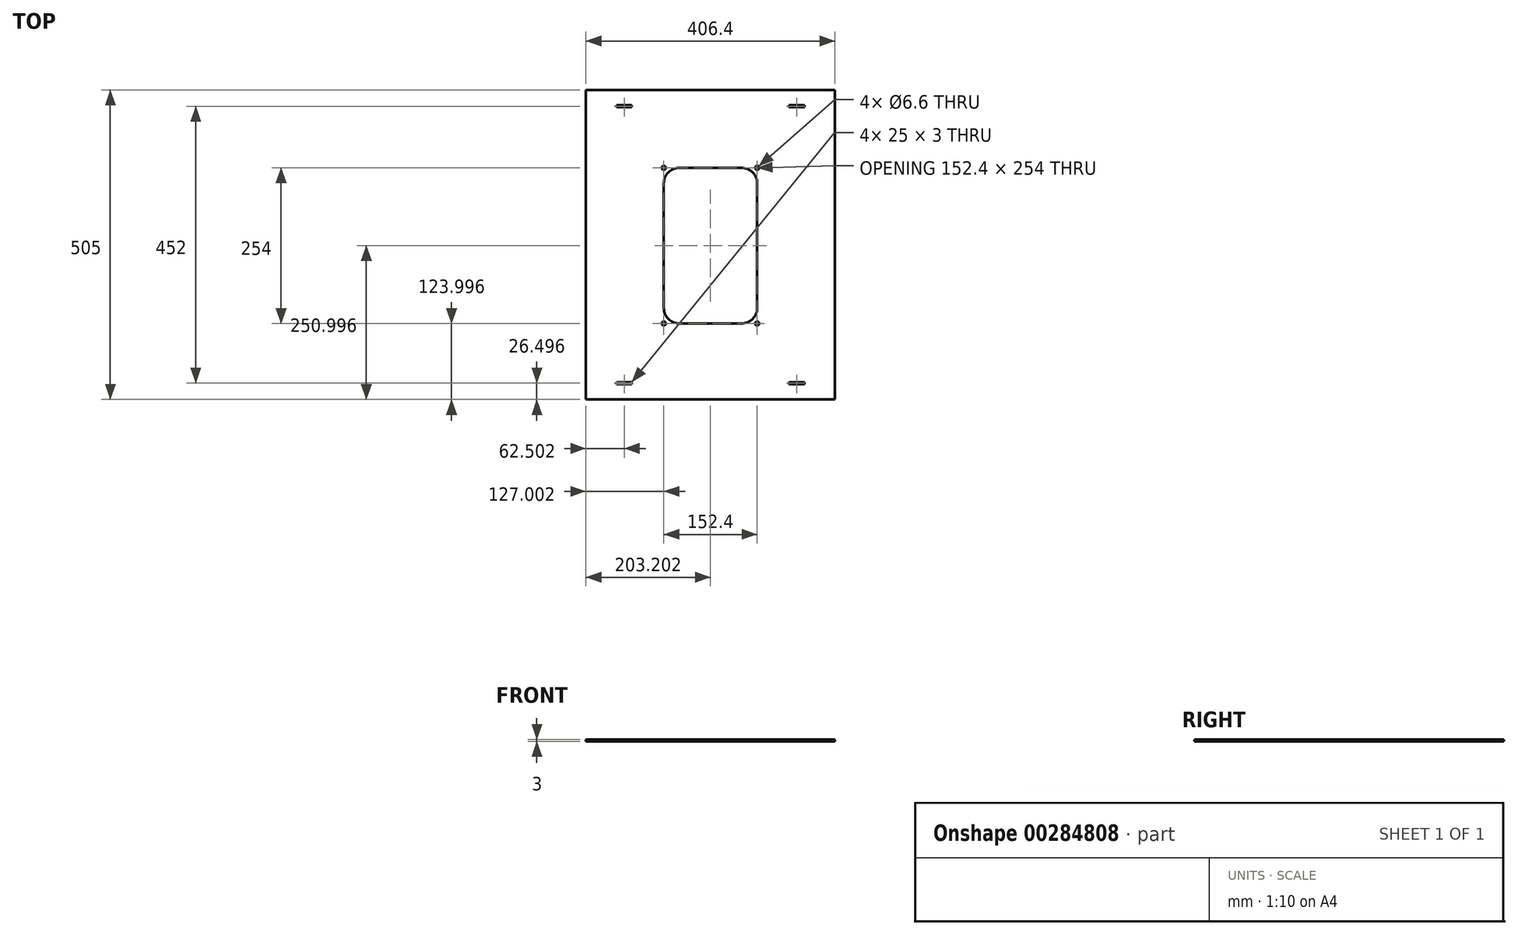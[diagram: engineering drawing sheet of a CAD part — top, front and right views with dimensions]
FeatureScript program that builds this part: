
annotation { "Feature Type Name" : "Feature", "Feature Type Description" : "" }
export const myFeature = defineFeature(function(context is Context, id is Id, definition is map)
    precondition{}
    {
        {
            var Q0;
            Q0=qCreatedBy(makeId("Top.planeOp"),FACE);
            var sketch = newSketch(context, id + "F0", { "sketchPlane" : qUnion([Q0])});
            skLineSegment(sketch, "E0.bottom", {"start": v(-241.68, 308.95) * mm, "end": v(164.72, 308.95) * mm});
            skLineSegment(sketch, "E0.top", {"start": v(-241.68, -196.05) * mm, "end": v(164.72, -196.05) * mm});
            skLineSegment(sketch, "E0.left", {"start": v(-241.68, 308.95) * mm, "end": v(-241.68, -196.05) * mm});
            skLineSegment(sketch, "E0.right", {"start": v(164.72, 308.95) * mm, "end": v(164.72, -196.05) * mm});
            skSolve(sketch);
        }
        {
            var Q0;
            Q0=qSketchRegion(id+"F0",true);
            extrude(context, id + "F1", {"entities" : qUnion([Q0]), "depth" : 3 * mm});
        }
        {
            var Q0;
            Q0=makeQuery(id+"F1.opExtrude","CAP_FACE",FACE,{"disambiguationData":[OSD([sQuery(id+"F0.wireOp",EDGE,"E0.bottom"),sQuery(id+"F0.wireOp",EDGE,"E0.top"),sQuery(id+"F0.wireOp",EDGE,"E0.left"),sQuery(id+"F0.wireOp",EDGE,"E0.right")])],"isStart":false});
            var sketch = newSketch(context, id + "F2", { "sketchPlane" : qUnion([Q0])});
            skLineSegment(sketch, "E1.bottom", {"start": v(-89.28, 181.95) * mm, "end": v(12.32, 181.95) * mm});
            skLineSegment(sketch, "E1.top", {"start": v(-89.28, -72.05) * mm, "end": v(12.32, -72.05) * mm});
            skLineSegment(sketch, "E1.left", {"start": v(-114.68, 156.55) * mm, "end": v(-114.68, -46.65) * mm});
            skLineSegment(sketch, "E1.right", {"start": v(37.72, 156.55) * mm, "end": v(37.72, -46.65) * mm});
            skPoint(sketch, "E2.visualSharp", {"position": v(-114.68, 181.95) * mm});
            skArc(sketch, "E2.filletArc", {"start": v(-89.28, 181.95) * mm, "mid": v(-107.24, 174.5) * mm, "end": v(-114.68, 156.55) * mm});
            skPoint(sketch, "E3.visualSharp", {"position": v(37.72, 181.95) * mm});
            skArc(sketch, "E3.filletArc", {"start": v(37.72, 156.55) * mm, "mid": v(30.28, 174.5) * mm, "end": v(12.32, 181.95) * mm});
            skPoint(sketch, "E4.visualSharp", {"position": v(37.72, -72.05) * mm});
            skArc(sketch, "E4.filletArc", {"start": v(12.32, -72.05) * mm, "mid": v(30.28, -64.61) * mm, "end": v(37.72, -46.65) * mm});
            skPoint(sketch, "E5.visualSharp", {"position": v(-114.68, -72.05) * mm});
            skArc(sketch, "E5.filletArc", {"start": v(-114.68, -46.65) * mm, "mid": v(-107.24, -64.61) * mm, "end": v(-89.28, -72.05) * mm});
            skSolve(sketch);
        }
        {
            var Q0;
            Q0=sQuery(id+"F2.wireOp",VERTEX,"E2.visualSharp");
            var Q1;
            Q1=sQuery(id+"F2.wireOp",VERTEX,"E3.visualSharp");
            var Q2;
            Q2=sQuery(id+"F2.wireOp",VERTEX,"E4.visualSharp");
            var Q3;
            Q3=sQuery(id+"F2.wireOp",VERTEX,"E5.visualSharp");
            var Q4;
            Q4=makeQuery(id+"F1.opExtrude","SWEPT_BODY",BODY,{"disambiguationData":[OSD([sQuery(id+"F0.wireOp",EDGE,"E0.bottom"),sQuery(id+"F0.wireOp",EDGE,"E0.top"),sQuery(id+"F0.wireOp",EDGE,"E0.left"),sQuery(id+"F0.wireOp",EDGE,"E0.right")])]});
            hole(context, id + "F3", {"style" : HoleStyle.SIMPLE, "endStyle" : HoleEndStyle.THROUGH, "standardTappedOrClearance" : lookupTablePath({ "standard" : "ISO", "fit" : "Normal", "size" : "M6", "type" : "Clearance" }), "standardBlindInLast" : lookupTablePath({ "fit" : "Standard", "standard" : "ISO", "size" : "M6", "type" : "Clearance" }), "holeDiameter" : 6.6 * mm, "tappedDepth" : 12 * mm, "tapClearance" : 3, "locations" : qUnion([Q0, Q1, Q2, Q3]), "scope" : qUnion([Q4])});
        }
        {
            var Q0;
            Q0 = qSketchRegion(id + "F2", true);
            extrude(context, id + "F4", {"entities" : qUnion([Q0]), "operationType" : NewBodyOperationType.REMOVE, "oppositeDirection" : true, "depth" : 25 * mm});
        }
        {
            var Q0;
            Q0=makeQuery(id+"F1.opExtrude","CAP_FACE",FACE,{"disambiguationData":[OSD([sQuery(id+"F0.wireOp",EDGE,"E0.bottom"),sQuery(id+"F0.wireOp",EDGE,"E0.top"),sQuery(id+"F0.wireOp",EDGE,"E0.left"),sQuery(id+"F0.wireOp",EDGE,"E0.right")])],"isStart":false});
            var sketch = newSketch(context, id + "F5", { "sketchPlane" : qUnion([Q0])});
            skLineSegment(sketch, "E6.bottom", {"start": v(-191.68, 283.95) * mm, "end": v(-166.68, 283.95) * mm});
            skLineSegment(sketch, "E6.top", {"start": v(-191.68, 280.95) * mm, "end": v(-166.68, 280.95) * mm});
            skLineSegment(sketch, "E6.left", {"start": v(-191.68, 283.95) * mm, "end": v(-191.68, 280.95) * mm});
            skLineSegment(sketch, "E6.right", {"start": v(-166.68, 283.95) * mm, "end": v(-166.68, 280.95) * mm});
            skLineSegment(sketch, "E7.bottom", {"start": v(89.72, 283.95) * mm, "end": v(114.72, 283.95) * mm});
            skLineSegment(sketch, "E7.top", {"start": v(89.72, 280.95) * mm, "end": v(114.72, 280.95) * mm});
            skLineSegment(sketch, "E7.left", {"start": v(89.72, 283.95) * mm, "end": v(89.72, 280.95) * mm});
            skLineSegment(sketch, "E7.right", {"start": v(114.72, 283.95) * mm, "end": v(114.72, 280.95) * mm});
            skLineSegment(sketch, "E8.bottom", {"start": v(89.72, -168.05) * mm, "end": v(114.72, -168.05) * mm});
            skLineSegment(sketch, "E8.top", {"start": v(89.72, -171.05) * mm, "end": v(114.72, -171.05) * mm});
            skLineSegment(sketch, "E8.left", {"start": v(89.72, -168.05) * mm, "end": v(89.72, -171.05) * mm});
            skLineSegment(sketch, "E8.right", {"start": v(114.72, -168.05) * mm, "end": v(114.72, -171.05) * mm});
            skLineSegment(sketch, "E9.bottom", {"start": v(-191.68, -168.05) * mm, "end": v(-166.68, -168.05) * mm});
            skLineSegment(sketch, "E9.top", {"start": v(-191.68, -171.05) * mm, "end": v(-166.68, -171.05) * mm});
            skLineSegment(sketch, "E9.left", {"start": v(-191.68, -168.05) * mm, "end": v(-191.68, -171.05) * mm});
            skLineSegment(sketch, "E9.right", {"start": v(-166.68, -168.05) * mm, "end": v(-166.68, -171.05) * mm});
            skSolve(sketch);
        }
        {
            var Q0;
            Q0 = qSketchRegion(id + "F5", true);
            extrude(context, id + "F6", {"entities" : qUnion([Q0]), "operationType" : NewBodyOperationType.REMOVE, "oppositeDirection" : true, "depth" : 25 * mm, "offsetDistance" : 25 * mm});
        }
    });
